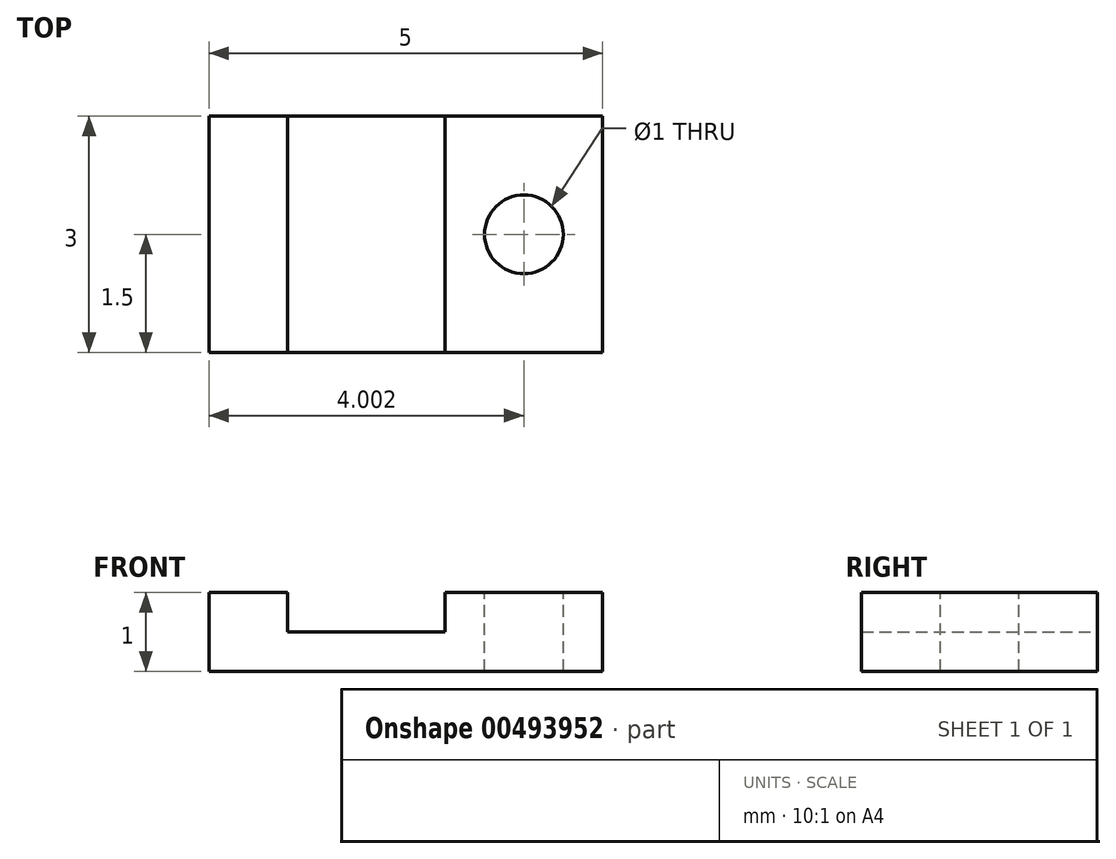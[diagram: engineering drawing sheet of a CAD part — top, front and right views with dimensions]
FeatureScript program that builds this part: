
annotation { "Feature Type Name" : "Feature", "Feature Type Description" : "" }
export const myFeature = defineFeature(function(context is Context, id is Id, definition is map)
    precondition{}
    {
        {
            var Q0;
            Q0=qCreatedBy(makeId("Front.planeOp"),FACE);
            var sketch = newSketch(context, id + "F0", { "sketchPlane" : qUnion([Q0])});
            skLineSegment(sketch, "E0", {"start": v(-3.39, 0) * mm, "end": v(1.61, 0) * mm});
            skLineSegment(sketch, "E1", {"start": v(1.61, 0) * mm, "end": v(1.61, 1) * mm});
            skLineSegment(sketch, "E2", {"start": v(1.61, 1) * mm, "end": v(-0.39, 1) * mm});
            skLineSegment(sketch, "E3", {"start": v(-0.39, 1) * mm, "end": v(-0.39, 0.5) * mm});
            skLineSegment(sketch, "E4", {"start": v(-0.39, 0.5) * mm, "end": v(-2.39, 0.5) * mm});
            skLineSegment(sketch, "E5", {"start": v(-2.39, 0.5) * mm, "end": v(-2.39, 1) * mm});
            skLineSegment(sketch, "E6", {"start": v(-2.39, 1) * mm, "end": v(-3.39, 1) * mm});
            skLineSegment(sketch, "E7", {"start": v(-3.39, 1) * mm, "end": v(-3.39, 0) * mm});
            skSolve(sketch);
        }
        {
            var Q0;
            Q0 = qSketchRegion(id + "F0", true);
            extrude(context, id + "F1", {"entities" : qUnion([Q0]), "depth" : 3 * mm});
        }
        {
            var Q0;
            Q0=makeQuery(id+"F1.opExtrude","SWEPT_FACE",FACE,{"disambiguationData":[OSD([sQuery(id+"F0.wireOp",EDGE,"E2")])]});
            var sketch = newSketch(context, id + "F2", { "sketchPlane" : qUnion([Q0])});
            skPoint(sketch, "E8", {"position": v(0.61, -1.5) * mm});
            skSolve(sketch);
        }
        {
            var Q0;
            Q0=sQuery(id+"F2.wireOp",VERTEX,"E8");
            var Q1;
            Q1=makeQuery(id+"F1.opExtrude","SWEPT_BODY",BODY,{"disambiguationData":[OSD([sQuery(id+"F0.wireOp",EDGE,"E0"),sQuery(id+"F0.wireOp",EDGE,"E1"),sQuery(id+"F0.wireOp",EDGE,"E2"),sQuery(id+"F0.wireOp",EDGE,"E3"),sQuery(id+"F0.wireOp",EDGE,"E4"),sQuery(id+"F0.wireOp",EDGE,"E5"),sQuery(id+"F0.wireOp",EDGE,"E6"),sQuery(id+"F0.wireOp",EDGE,"E7")])]});
            hole(context, id + "F3", {"style" : HoleStyle.SIMPLE, "endStyle" : HoleEndStyle.THROUGH, "holeDiameter" : 1 * mm, "isTappedThrough" : true, "tappedDepth" : 12 * mm, "tapClearance" : 3, "locations" : qUnion([Q0]), "scope" : qUnion([Q1])});
        }
    });
